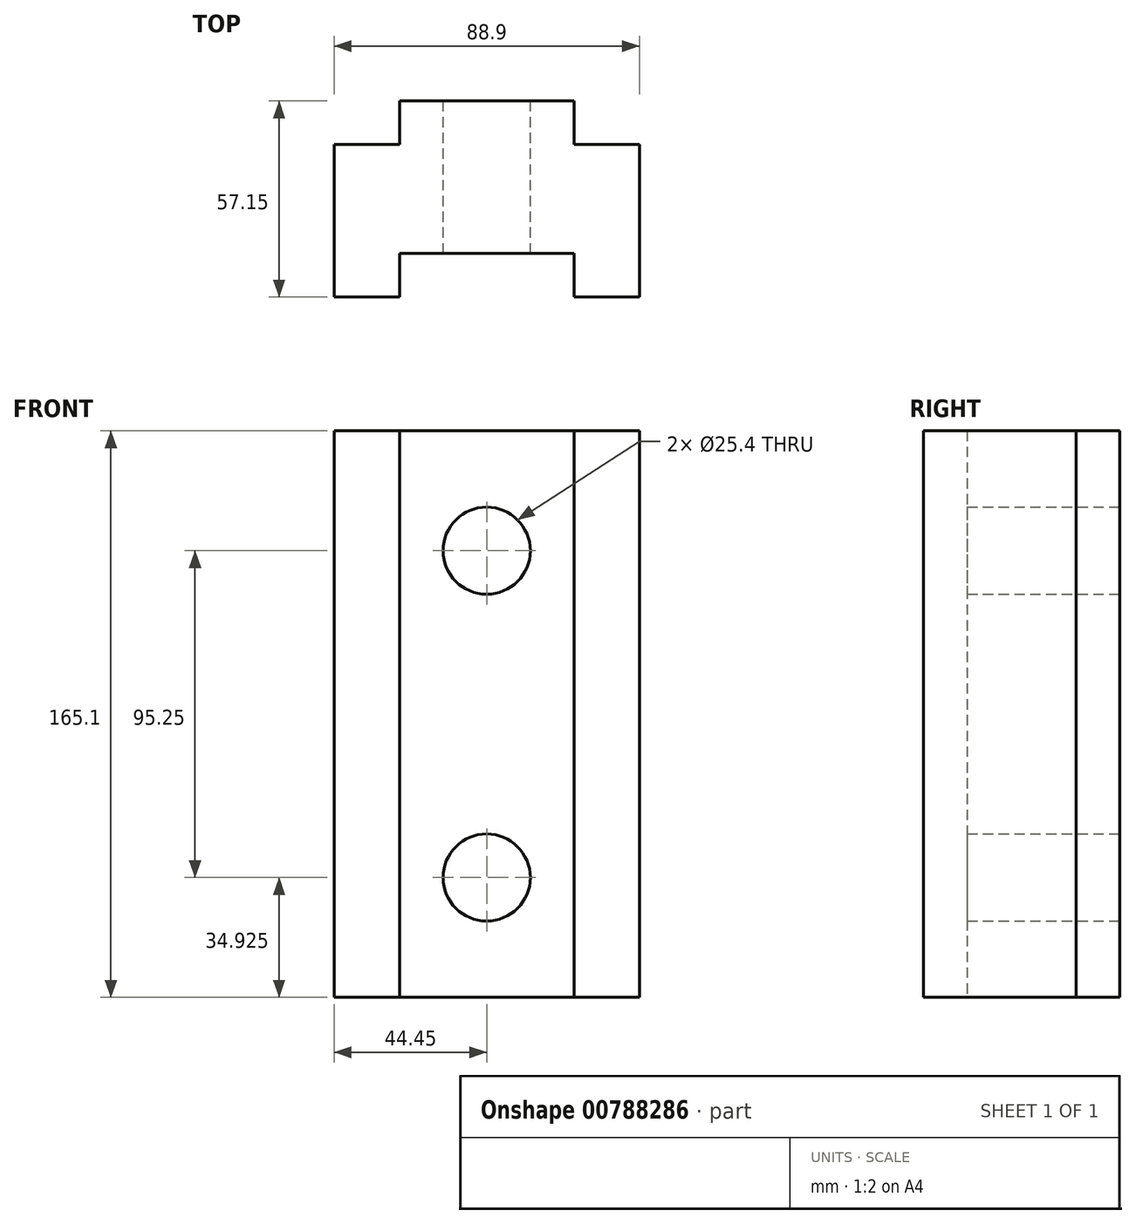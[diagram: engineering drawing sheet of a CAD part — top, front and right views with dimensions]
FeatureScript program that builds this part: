
annotation { "Feature Type Name" : "Feature", "Feature Type Description" : "" }
export const myFeature = defineFeature(function(context is Context, id is Id, definition is map)
    precondition{}
    {
        {
            var Q0;
            Q0=qCreatedBy(makeId("Top.planeOp"),FACE);
            var sketch = newSketch(context, id + "F0", { "sketchPlane" : qUnion([Q0])});
            skLineSegment(sketch, "E0", {"start": v(0, 0) * mm, "end": v(-19.05, 0) * mm});
            skLineSegment(sketch, "E1", {"start": v(50.8, 0) * mm, "end": v(69.85, 0) * mm});
            skLineSegment(sketch, "E2", {"start": v(69.85, 0) * mm, "end": v(69.85, 44.45) * mm});
            skLineSegment(sketch, "E3", {"start": v(69.85, 44.45) * mm, "end": v(50.8, 44.45) * mm});
            skLineSegment(sketch, "E4", {"start": v(50.8, 44.45) * mm, "end": v(50.8, 57.15) * mm});
            skLineSegment(sketch, "E5", {"start": v(50.8, 57.15) * mm, "end": v(0, 57.15) * mm});
            skLineSegment(sketch, "E6", {"start": v(0, 57.15) * mm, "end": v(0, 44.45) * mm});
            skLineSegment(sketch, "E7", {"start": v(0, 44.45) * mm, "end": v(-19.05, 44.45) * mm});
            skLineSegment(sketch, "E8", {"start": v(-19.05, 44.45) * mm, "end": v(-19.05, 0) * mm});
            skLineSegment(sketch, "E9", {"start": v(0, 0) * mm, "end": v(0, 12.7) * mm});
            skLineSegment(sketch, "E10", {"start": v(0, 12.7) * mm, "end": v(50.8, 12.7) * mm});
            skLineSegment(sketch, "E11", {"start": v(50.8, 12.7) * mm, "end": v(50.8, 0) * mm});
            skSolve(sketch);
        }
        {
            var Q0;
            Q0=makeQuery(id+"F0.imprint","IMPRINT",FACE,{"disambiguationData":[TD([[makeQuery(id+"F0.imprint","IMPRINT",EDGE,{"derivedFrom":sQuery(id+"F0.wireOp",EDGE,"E0")}),-1.0]])]});
            extrude(context, id + "F1", {"entities" : qUnion([Q0]), "depth" : 25.4 * mm, "offsetDistance" : 25.4 * mm});
        }
        {
            var Q0;
            Q0=makeQuery(id+"F1.opExtrude","CAP_FACE",FACE,{"disambiguationData":[OSD([sQuery(id+"F0.wireOp",EDGE,"E0"),sQuery(id+"F0.wireOp",EDGE,"E1"),sQuery(id+"F0.wireOp",EDGE,"E2"),sQuery(id+"F0.wireOp",EDGE,"E3"),sQuery(id+"F0.wireOp",EDGE,"E4"),sQuery(id+"F0.wireOp",EDGE,"E5"),sQuery(id+"F0.wireOp",EDGE,"E6"),sQuery(id+"F0.wireOp",EDGE,"E7"),sQuery(id+"F0.wireOp",EDGE,"E8"),sQuery(id+"F0.wireOp",EDGE,"E9"),sQuery(id+"F0.wireOp",EDGE,"E10"),sQuery(id+"F0.wireOp",EDGE,"E11")])],"isStart":false});
            extrude(context, id + "F2", {"entities" : qUnion([Q0]), "operationType" : NewBodyOperationType.ADD, "depth" : 139.7 * mm, "offsetDistance" : 25.4 * mm});
        }
        {
            var Q0;
            {var subQ0=sQuery(id+"F0.wireOp",EDGE,"E5");Q0=makeQuery(id+"F2.boolean.opBoolean","MERGE",FACE,{"derivedFrom":[makeQuery(id+"F1.opExtrude","SWEPT_FACE",FACE,{"disambiguationData":[OSD([subQ0])]}),makeQuery(id+"F2.opExtrude","SWEPT_FACE",FACE,{"disambiguationData":[OSD([subQ0])]})]});}
            var sketch = newSketch(context, id + "F3", { "sketchPlane" : qUnion([Q0])});
            skLineSegment(sketch, "E12", {"start": v(-25.4, 0) * mm, "end": v(-25.4, 34.93) * mm, "construction": true});
            skLineSegment(sketch, "E13", {"start": v(-25.4, 165.1) * mm, "end": v(-25.4, 130.18) * mm, "construction": true});
            skCircle(sketch, "E14", {"center": v(-25.4, 130.18) * mm, "radius": 12.7 * mm});
            skCircle(sketch, "E15", {"center": v(-25.4, 34.93) * mm, "radius": 12.7 * mm});
            skSolve(sketch);
        }
        {
            var Q0;
            Q0=makeQuery(id+"F3.imprint","IMPRINT",FACE,{"disambiguationData":[TD([[makeQuery(id+"F3.imprint","IMPRINT",EDGE,{"derivedFrom":sQuery(id+"F3.wireOp",EDGE,"E14")}),1.0]])]});
            extrude(context, id + "F4", {"entities" : qUnion([Q0]), "operationType" : NewBodyOperationType.REMOVE, "endBound" : BoundingType.UP_TO_NEXT, "oppositeDirection" : true, "depth" : 25.4 * mm, "offsetDistance" : 25.4 * mm});
        }
        {
            var Q0;
            Q0=makeQuery(id+"F3.imprint","IMPRINT",FACE,{"disambiguationData":[TD([[makeQuery(id+"F3.imprint","IMPRINT",EDGE,{"derivedFrom":sQuery(id+"F3.wireOp",EDGE,"E15")}),1.0]])]});
            extrude(context, id + "F5", {"entities" : qUnion([Q0]), "operationType" : NewBodyOperationType.REMOVE, "endBound" : BoundingType.UP_TO_NEXT, "oppositeDirection" : true, "depth" : 25.4 * mm, "offsetDistance" : 25.4 * mm});
        }
    });
